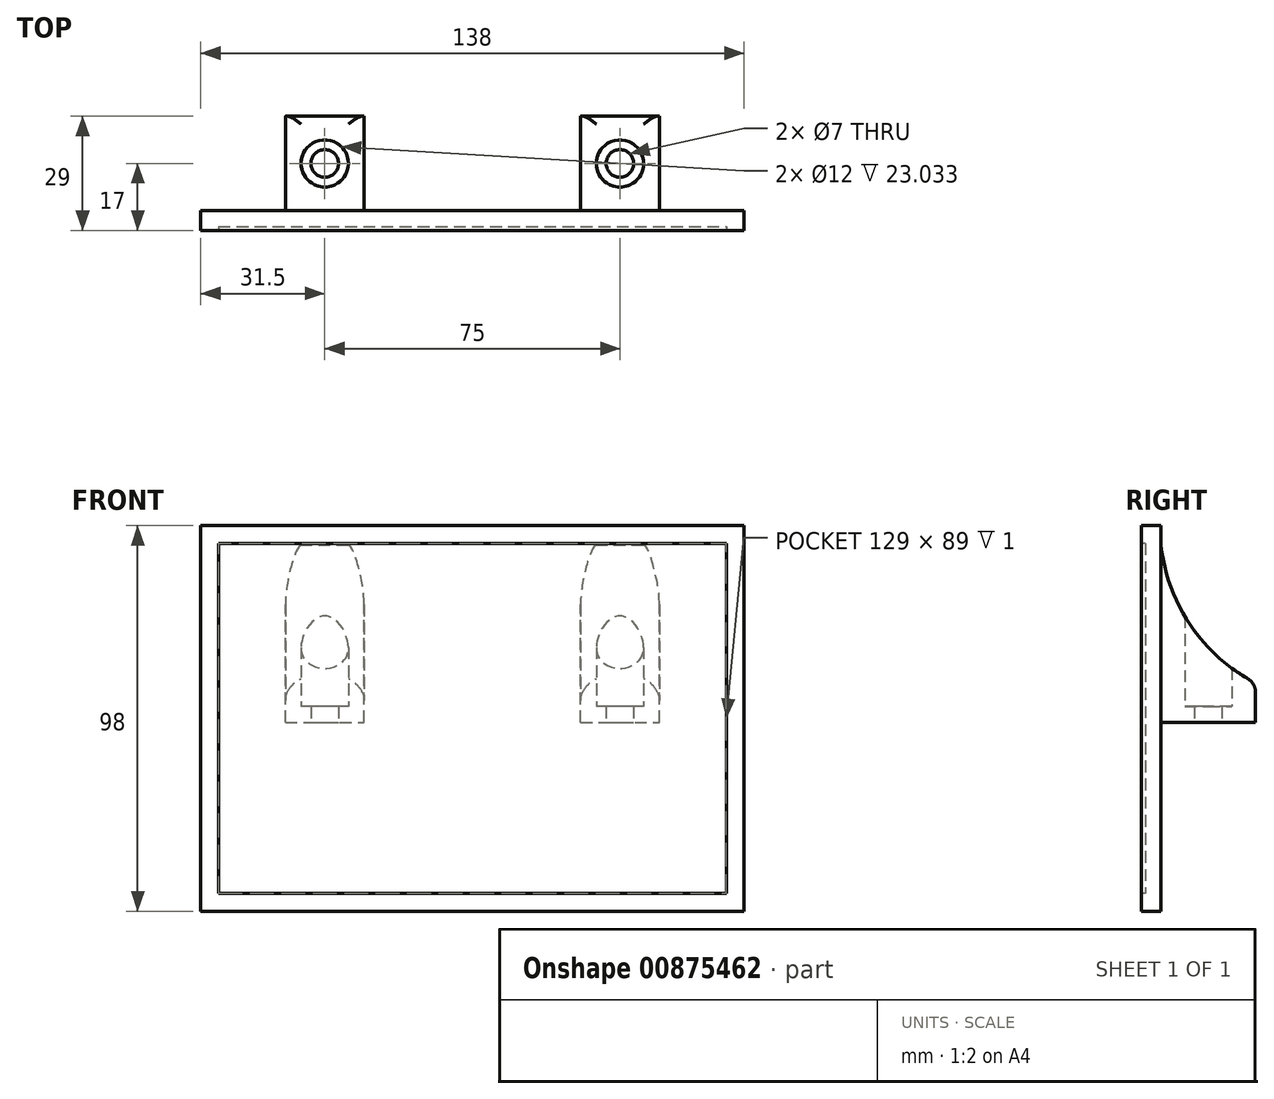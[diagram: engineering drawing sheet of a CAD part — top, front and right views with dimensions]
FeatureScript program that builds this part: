
annotation { "Feature Type Name" : "Feature", "Feature Type Description" : "" }
export const myFeature = defineFeature(function(context is Context, id is Id, definition is map)
    precondition{}
    {
        {
            var Q0;
            Q0=qCreatedBy(makeId("Front.planeOp"),FACE);
            var sketch = newSketch(context, id + "F0", { "sketchPlane" : qUnion([Q0])});
            skLineSegment(sketch, "E0.bottom", {"start": v(-69, 49) * mm, "end": v(69, 49) * mm});
            skLineSegment(sketch, "E0.top", {"start": v(-69, -49) * mm, "end": v(69, -49) * mm});
            skLineSegment(sketch, "E0.left", {"start": v(-69, 49) * mm, "end": v(-69, -49) * mm});
            skLineSegment(sketch, "E0.right", {"start": v(69, 49) * mm, "end": v(69, -49) * mm});
            skPoint(sketch, "E0.middle", {"position": v(0, 0) * mm});
            skSolve(sketch);
        }
        {
            var Q0;
            Q0 = qSketchRegion(id + "F0", true);
            extrude(context, id + "F1", {"entities" : qUnion([Q0]), "depth" : 5 * mm, "offsetDistance" : 25 * mm});
        }
        {
            var Q0;
            Q0=makeQuery(id+"F1.opExtrude","CAP_FACE",FACE,{"disambiguationData":[OSD([sQuery(id+"F0.wireOp",EDGE,"E0.bottom"),sQuery(id+"F0.wireOp",EDGE,"E0.top"),sQuery(id+"F0.wireOp",EDGE,"E0.left"),sQuery(id+"F0.wireOp",EDGE,"E0.right")])],"isStart":false});
            var sketch = newSketch(context, id + "F2", { "sketchPlane" : qUnion([Q0])});
            skLineSegment(sketch, "E1.bottom", {"start": v(-64.5, 44.5) * mm, "end": v(64.5, 44.5) * mm});
            skLineSegment(sketch, "E1.top", {"start": v(-64.5, -44.5) * mm, "end": v(64.5, -44.5) * mm});
            skLineSegment(sketch, "E1.left", {"start": v(-64.5, 44.5) * mm, "end": v(-64.5, -44.5) * mm});
            skLineSegment(sketch, "E1.right", {"start": v(64.5, 44.5) * mm, "end": v(64.5, -44.5) * mm});
            skPoint(sketch, "E1.middle", {"position": v(0, 0) * mm});
            skLineSegment(sketch, "E2", {"start": v(0, 44.5) * mm, "end": v(0, 49) * mm, "construction": true});
            skLineSegment(sketch, "E3", {"start": v(-64.5, 0) * mm, "end": v(-69, 0) * mm, "construction": true});
            skLineSegment(sketch, "E4", {"start": v(0, -44.5) * mm, "end": v(0, -49) * mm, "construction": true});
            skLineSegment(sketch, "E5", {"start": v(64.5, 0) * mm, "end": v(69, 0) * mm, "construction": true});
            skSolve(sketch);
        }
        {
            var Q0;
            Q0 = qSketchRegion(id + "F2", true);
            extrude(context, id + "F3", {"entities" : qUnion([Q0]), "operationType" : NewBodyOperationType.REMOVE, "oppositeDirection" : true, "depth" : 1 * mm, "offsetDistance" : 25 * mm});
        }
        {
            var Q0;
            Q0=makeQuery(id+"F1.opExtrude","SWEPT_FACE",FACE,{"disambiguationData":[OSD([sQuery(id+"F0.wireOp",EDGE,"E0.top")])]});
            cPlane(context, id + "F4", {"entities" : qUnion([Q0]), "cplaneType" : CPlaneType.OFFSET, "offset" : 48 * mm, "oppositeDirection" : true, "width" : 150 * mm, "height" : 150 * mm});
        }
        {
            var Q0;
            Q0=qCreatedBy(id+"F4.planeOp",FACE);
            var sketch = newSketch(context, id + "F5", { "sketchPlane" : qUnion([Q0])});
            skLineSegment(sketch, "E6.bottom", {"start": v(-69, 0) * mm, "end": v(69, 0) * mm});
            skLineSegment(sketch, "E6.top", {"start": v(-69, -24) * mm, "end": v(69, -24) * mm});
            skLineSegment(sketch, "E6.left", {"start": v(-69, 0) * mm, "end": v(-69, -24) * mm});
            skLineSegment(sketch, "E6.right", {"start": v(69, 0) * mm, "end": v(69, -24) * mm});
            skLineSegment(sketch, "E7", {"start": v(-69, -12) * mm, "end": v(69, -12) * mm, "construction": true});
            skCircle(sketch, "E8", {"center": v(-37.5, -12) * mm, "radius": 3.5 * mm});
            skCircle(sketch, "E9", {"center": v(37.5, -12) * mm, "radius": 3.5 * mm});
            skLineSegment(sketch, "E10", {"start": v(-37.5, -15.5) * mm, "end": v(37.5, -15.5) * mm, "construction": true});
            skPoint(sketch, "E11", {"position": v(0, -15.5) * mm});
            skSolve(sketch);
        }
        {
            var Q0;
            Q0 = qSketchRegion(id + "F5", true);
            extrude(context, id + "F6", {"entities" : qUnion([Q0]), "operationType" : NewBodyOperationType.ADD, "oppositeDirection" : true, "depth" : 10 * mm, "offsetDistance" : 25 * mm});
        }
        {
            var Q0;
            Q0=makeQuery(id+"F6.opExtrude","CAP_FACE",FACE,{"disambiguationData":[OSD([sQuery(id+"F5.wireOp",EDGE,"E6.bottom"),sQuery(id+"F5.wireOp",EDGE,"E6.top"),sQuery(id+"F5.wireOp",EDGE,"E6.left"),sQuery(id+"F5.wireOp",EDGE,"E6.right"),sQuery(id+"F5.wireOp",EDGE,"E8"),sQuery(id+"F5.wireOp",EDGE,"E9")])],"isStart":false});
            var sketch = newSketch(context, id + "F7", { "sketchPlane" : qUnion([Q0])});
            skCircle(sketch, "E12", {"center": v(37.5, 12) * mm, "radius": 6 * mm});
            skCircle(sketch, "E13", {"center": v(-37.5, 12) * mm, "radius": 6 * mm});
            skSolve(sketch);
        }
        {
            var Q0;
            Q0=qCreatedBy(makeId("Right.planeOp"),FACE);
            cPlane(context, id + "F8", {"entities" : qUnion([Q0]), "cplaneType" : CPlaneType.OFFSET, "offset" : (75 / 2) * mm, "width" : 150 * mm, "height" : 150 * mm});
        }
        {
            var Q0;
            Q0=qCreatedBy(makeId("Right.planeOp"),FACE);
            cPlane(context, id + "F9", {"entities" : qUnion([Q0]), "cplaneType" : CPlaneType.OFFSET, "offset" : (75 / 2) * mm, "oppositeDirection" : true, "width" : 150 * mm, "height" : 150 * mm});
        }
        {
            var Q0;
            Q0=qCreatedBy(id+"F8.planeOp",FACE);
            var sketch = newSketch(context, id + "F10", { "sketchPlane" : qUnion([Q0])});
            skArc(sketch, "E14", {"start": v(0, 44) * mm, "mid": v(7.62, 23.5) * mm, "end": v(24, 9) * mm});
            skLineSegment(sketch, "E15", {"start": v(24, 9) * mm, "end": v(24, 8) * mm});
            skLineSegment(sketch, "E16", {"start": v(24, 8) * mm, "end": v(-1, 8) * mm});
            skLineSegment(sketch, "E17", {"start": v(-1, 8) * mm, "end": v(-1, 44) * mm});
            skLineSegment(sketch, "E18", {"start": v(-1, 44) * mm, "end": v(0, 44) * mm});
            skSolve(sketch);
        }
        {
            var Q0;
            Q0 = qSketchRegion(id + "F10", true);
            extrude(context, id + "F11", {"entities" : qUnion([Q0]), "operationType" : NewBodyOperationType.ADD, "depth" : 10 * mm, "offsetDistance" : 25 * mm, "hasSecondDirection" : true, "secondDirectionOppositeDirection" : true, "secondDirectionDepth" : 10 * mm});
        }
        {
            var Q0;
            Q0=qCreatedBy(id+"F9.planeOp",FACE);
            var sketch = newSketch(context, id + "F12", { "sketchPlane" : qUnion([Q0])});
            skArc(sketch, "E19", {"start": v(0, 44) * mm, "mid": v(7.62, 23.5) * mm, "end": v(24, 9) * mm});
            skLineSegment(sketch, "E20", {"start": v(24, 9) * mm, "end": v(24, 7.7) * mm});
            skLineSegment(sketch, "E21", {"start": v(24, 7.7) * mm, "end": v(-1.1, 7.7) * mm});
            skLineSegment(sketch, "E22", {"start": v(-1.1, 7.7) * mm, "end": v(-1.1, 44) * mm});
            skLineSegment(sketch, "E23", {"start": v(-1.1, 44) * mm, "end": v(0, 44) * mm});
            skSolve(sketch);
        }
        {
            var Q0;
            Q0 = qSketchRegion(id + "F12", true);
            extrude(context, id + "F13", {"entities" : qUnion([Q0]), "operationType" : NewBodyOperationType.ADD, "depth" : 10 * mm, "offsetDistance" : 25 * mm, "hasSecondDirection" : true, "secondDirectionOppositeDirection" : true, "secondDirectionDepth" : 10 * mm});
        }
        {
            var Q0;
            Q0 = qSketchRegion(id + "F7", true);
            extrude(context, id + "F14", {"entities" : qUnion([Q0]), "operationType" : NewBodyOperationType.REMOVE, "endBound" : BoundingType.THROUGH_ALL, "depth" : 25 * mm, "offsetDistance" : 25 * mm, "hasSecondDirection" : true, "secondDirectionOppositeDirection" : true, "secondDirectionDepth" : 6 * mm});
        }
        {
            var Q0;
            {var subQ0=sQuery(id+"F5.wireOp",EDGE,"E6.right");var subQ1=sQuery(id+"F0.wireOp",EDGE,"E0.right");var subQ2=sQuery(id+"F5.wireOp",EDGE,"E6.top");Q0=makeQuery(id+"F11.boolean.opBoolean","SPLIT",FACE,{"disambiguationData":[TD([makeQuery(id+"F1.opExtrude","SWEPT_FACE",FACE,{"disambiguationData":[OSD([subQ1])]})])],"derivedFrom":makeQuery(id+"F6.opExtrude","CAP_FACE",FACE,{"disambiguationData":[OSD([sQuery(id+"F5.wireOp",EDGE,"E6.bottom"),subQ2,sQuery(id+"F5.wireOp",EDGE,"E6.left"),subQ0,sQuery(id+"F5.wireOp",EDGE,"E8"),sQuery(id+"F5.wireOp",EDGE,"E9")])],"isStart":false})});}
            var sketch = newSketch(context, id + "F15", { "sketchPlane" : qUnion([Q0])});
            skLineSegment(sketch, "E24.bottom", {"start": v(-47.5, 0) * mm, "end": v(-69, 0) * mm});
            skLineSegment(sketch, "E24.top", {"start": v(-47.5, 24) * mm, "end": v(-69, 24) * mm});
            skLineSegment(sketch, "E24.left", {"start": v(-47.5, 0) * mm, "end": v(-47.5, 24) * mm});
            skLineSegment(sketch, "E24.right", {"start": v(-69, 0) * mm, "end": v(-69, 24) * mm});
            skLineSegment(sketch, "E25.bottom", {"start": v(-27.5, 24) * mm, "end": v(27.5, 24) * mm});
            skLineSegment(sketch, "E25.top", {"start": v(-27.5, 0) * mm, "end": v(27.5, 0) * mm});
            skLineSegment(sketch, "E25.left", {"start": v(-27.5, 24) * mm, "end": v(-27.5, 0) * mm});
            skLineSegment(sketch, "E25.right", {"start": v(27.5, 24) * mm, "end": v(27.5, 0) * mm});
            skLineSegment(sketch, "E26.bottom", {"start": v(47.5, 0) * mm, "end": v(69, 0) * mm});
            skLineSegment(sketch, "E26.top", {"start": v(47.5, 24) * mm, "end": v(69, 24) * mm});
            skLineSegment(sketch, "E26.left", {"start": v(47.5, 0) * mm, "end": v(47.5, 24) * mm});
            skLineSegment(sketch, "E26.right", {"start": v(69, 0) * mm, "end": v(69, 24) * mm});
            skSolve(sketch);
        }
        {
            var Q0;
            Q0 = qSketchRegion(id + "F15", true);
            extrude(context, id + "F16", {"entities" : qUnion([Q0]), "operationType" : NewBodyOperationType.REMOVE, "oppositeDirection" : true, "depth" : 25 * mm, "offsetDistance" : 25 * mm});
        }
        {
            var Q0;
            Q0=makeQuery(id+"F13.opExtrude","CAP_EDGE",EDGE,{"disambiguationData":[OSD([sQuery(id+"F12.wireOp",EDGE,"E19")])],"isStart":true});
            var Q1;
            Q1=makeQuery(id+"F13.opExtrude","CAP_EDGE",EDGE,{"disambiguationData":[OSD([sQuery(id+"F12.wireOp",EDGE,"E19")])],"isStart":false});
            var Q2;
            {var subQ1=sQuery(id+"F5.wireOp",EDGE,"E6.top");Q2=makeQuery(id+"F13.boolean.opBoolean","MERGE",EDGE,{"derivedFrom":[makeQuery(id+"F11.boolean.opBoolean","SPLIT",EDGE,{"disambiguationData":[TD([makeQuery(id+"F1.opExtrude","SWEPT_FACE",FACE,{"disambiguationData":[OSD([sQuery(id+"F0.wireOp",EDGE,"E0.left")])]})])],"derivedFrom":makeQuery(id+"F6.opExtrude","CAP_EDGE",EDGE,{"disambiguationData":[OSD([subQ1])],"isStart":false})}),makeQuery(id+"F13.opExtrude","SWEPT_EDGE",EDGE,{"disambiguationData":[OSD([sQuery(id+"F12.wireOp",EDGE,"E19"),sQuery(id+"F12.wireOp",EDGE,"E20")])]})]});}
            var Q3;
            Q3=makeQuery(id+"F11.opExtrude","CAP_EDGE",EDGE,{"disambiguationData":[OSD([sQuery(id+"F10.wireOp",EDGE,"E14")])],"isStart":false});
            var Q4;
            Q4=makeQuery(id+"F11.boolean.opBoolean","MERGE",EDGE,{"derivedFrom":[makeQuery(id+"F6.opExtrude","CAP_EDGE",EDGE,{"disambiguationData":[OSD([sQuery(id+"F5.wireOp",EDGE,"E6.top")])],"isStart":false}),makeQuery(id+"F11.opExtrude","SWEPT_EDGE",EDGE,{"disambiguationData":[OSD([sQuery(id+"F10.wireOp",EDGE,"E14"),sQuery(id+"F10.wireOp",EDGE,"E15")])]})]});
            var Q5;
            Q5=makeQuery(id+"F11.opExtrude","CAP_EDGE",EDGE,{"disambiguationData":[OSD([sQuery(id+"F10.wireOp",EDGE,"E14")])],"isStart":true});
            fillet(context, id + "F17", {"entities" : qUnion([Q0, Q1, Q2, Q3, Q4, Q5]), "radius" : 4 * mm, "tangentPropagation" : true, "allowEdgeOverflow" : false});
        }
    });
